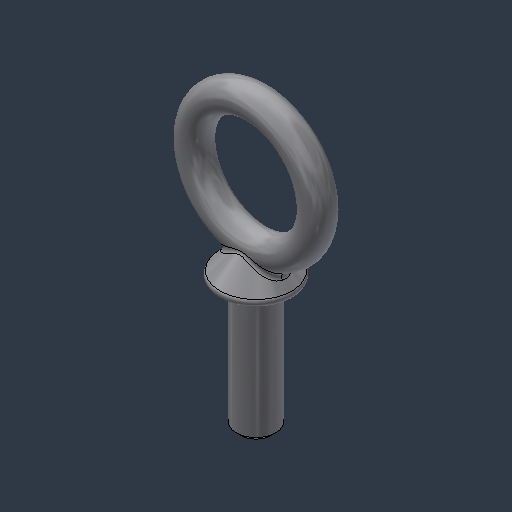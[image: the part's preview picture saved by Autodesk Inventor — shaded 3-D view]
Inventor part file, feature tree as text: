
AUTODESK INVENTOR PART (.ipt)
format: ipt  version: 2024.3 (Build 283343000, 343)  size: 211,456 bytes
history: native  units: mm (DEFAULTED — no unit token found)
features: fillet x1
ambient origin geometry x8: Origin, YZ Plane, XZ Plane, XY Plane, X Axis, Y Axis, Z Axis, Center Point
bodies: Solid1 (feature_tree)
feature tree (1):
  fillet  "Fillet1"  [1 undecoded]
note: 1 required parameter value undecoded (feature->parameter linkage not recoverable at this tier; creation-order binding heuristic only, values carry confidence <= 0.55)
